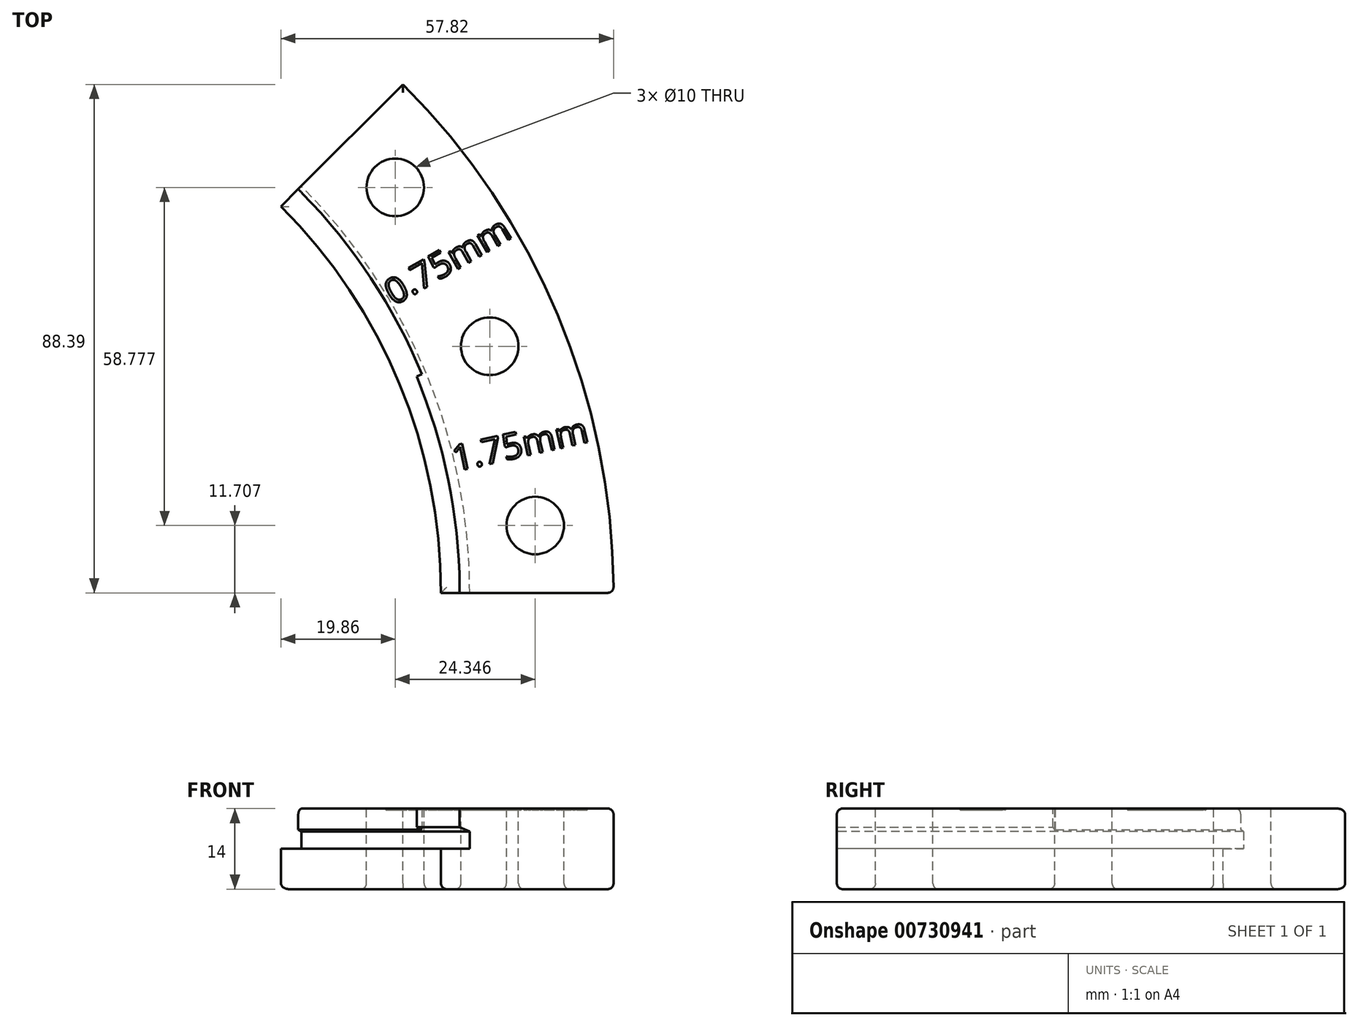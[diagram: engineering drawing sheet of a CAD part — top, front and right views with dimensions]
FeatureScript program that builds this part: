
annotation { "Feature Type Name" : "Feature", "Feature Type Description" : "" }
export const myFeature = defineFeature(function(context is Context, id is Id, definition is map)
    precondition{}
    {
        {
            var Q0;
            Q0=qCreatedBy(makeId("Top.planeOp"),FACE);
            var sketch = newSketch(context, id + "F0", { "sketchPlane" : qUnion([Q0])});
            skCircle(sketch, "E0", {"center": v(0, 0) * mm, "radius": 100 * mm});
            skSolve(sketch);
        }
        {
            var Q0;
            Q0=qCreatedBy(makeId("Front.planeOp"),FACE);
            var sketch = newSketch(context, id + "F1", { "sketchPlane" : qUnion([Q0])});
            skLineSegment(sketch, "E1.0", {"start": v(-100, 0) * mm, "end": v(100, 0) * mm});
            skLineSegment(sketch, "E2", {"start": v(100, 4) * mm, "end": v(97.75, 4) * mm});
            skLineSegment(sketch, "E3", {"start": v(125, 4) * mm, "end": v(100, 4) * mm});
            skLineSegment(sketch, "E4", {"start": v(100, 0) * mm, "end": v(100, -3) * mm});
            skLineSegment(sketch, "E5", {"start": v(100, -10) * mm, "end": v(125, -10) * mm});
            skLineSegment(sketch, "E6", {"start": v(125, -10) * mm, "end": v(125, 4) * mm});
            skLineSegment(sketch, "E7", {"start": v(0, 0) * mm, "end": v(0, 50.74) * mm});
            skLineSegment(sketch, "E8", {"start": v(100, -10) * mm, "end": v(95, -10) * mm});
            skLineSegment(sketch, "E9", {"start": v(95, -10) * mm, "end": v(95, -3) * mm});
            skLineSegment(sketch, "E10", {"start": v(95, -3) * mm, "end": v(100, -3) * mm});
            skLineSegment(sketch, "E11", {"start": v(97.75, 4) * mm, "end": v(97.75, 1) * mm});
            skLineSegment(sketch, "E12", {"start": v(100, 0) * mm, "end": v(97.75, 1) * mm});
            skSolve(sketch);
        }
        {
            var Q0;
            Q0=makeQuery(id+"F1.imprint","IMPRINT",FACE,{"disambiguationData":[TD([[makeQuery(id+"F1.imprint","IMPRINT",EDGE,{"derivedFrom":sQuery(id+"F1.wireOp",EDGE,"E2")}),1.0]])]});
            var Q1;
            Q1=sQuery(id+"F1.wireOp",EDGE,"E7");
            revolve(context, id + "F2", {"entities" : qUnion([Q0]), "axis" : qUnion([Q1]), "revolveType" : RevolveType.ONE_DIRECTION, "angle" : 45 * degree});
        }
        {
            var Q0;
            Q0=makeQuery(id+"F2.opRevolve","CAP_FACE",FACE,{"disambiguationData":[OSD([sQuery(id+"F1.wireOp",EDGE,"E2"),sQuery(id+"F1.wireOp",EDGE,"E3"),sQuery(id+"F1.wireOp",EDGE,"E4"),sQuery(id+"F1.wireOp",EDGE,"E5"),sQuery(id+"F1.wireOp",EDGE,"E6"),sQuery(id+"F1.wireOp",EDGE,"E8"),sQuery(id+"F1.wireOp",EDGE,"E9"),sQuery(id+"F1.wireOp",EDGE,"E10"),sQuery(id+"F1.wireOp",EDGE,"E11"),sQuery(id+"F1.wireOp",EDGE,"E12")])],"isStart":false});
            var sketch = newSketch(context, id + "F3", { "sketchPlane" : qUnion([Q0])});
            skLineSegment(sketch, "E13", {"start": v(0, 0) * mm, "end": v(0, 46.88) * mm});
            skLineSegment(sketch, "E14.0", {"start": v(-99.25, 0.33) * mm, "end": v(-97.75, 1) * mm});
            skLineSegment(sketch, "E15.0", {"start": v(-97.75, 4) * mm, "end": v(-97.75, 1) * mm});
            skLineSegment(sketch, "E16.0", {"start": v(-99.25, 4) * mm, "end": v(-97.75, 4) * mm});
            skLineSegment(sketch, "E17", {"start": v(-99.25, 4) * mm, "end": v(-99.25, 0.33) * mm});
            skLineSegment(sketch, "E18", {"start": v(-97.75, 4) * mm, "end": v(-99.25, 4) * mm});
            skPoint(sketch, "E19.start.orphan", {"position": v(-100, 0) * mm});
            skPoint(sketch, "E20.orphan", {"position": v(-125, 4) * mm});
            skLineSegment(sketch, "E21", {"start": v(-98.25, 4) * mm, "end": v(-98.25, 0.78) * mm});
            skSolve(sketch);
        }
        {
            var Q0;
            Q0=makeQuery(id+"F3.imprint","IMPRINT",FACE,{"disambiguationData":[TD([[makeQuery(id+"F3.imprint","IMPRINT",EDGE,{"derivedFrom":sQuery(id+"F3.wireOp",EDGE,"E15.0")}),-1.0]])]});
            var Q1;
            {var subQ0=sQuery(id+"F3.wireOp",EDGE,"E17");Q1=makeQuery(id+"F3.imprint","IMPRINT",FACE,{"disambiguationData":[TD([[makeQuery(id+"F3.imprint","IMPRINT",EDGE,{"derivedFrom":subQ0}),1.0]])]});}
            var Q2;
            Q2=sQuery(id+"F3.wireOp",EDGE,"E13");
            revolve(context, id + "F4", {"operationType" : NewBodyOperationType.REMOVE, "entities" : qUnion([Q0, Q1]), "axis" : qUnion([Q2]), "revolveType" : RevolveType.ONE_DIRECTION, "oppositeDirection" : true, "angle" : 22.5 * degree, "surfaceOperationType" : NewSurfaceOperationType.NEW});
        }
        {
            var Q0;
            {var subQ0=sQuery(id+"F3.wireOp",EDGE,"E15.0");Q0=makeQuery(id+"F3.imprint","IMPRINT",FACE,{"disambiguationData":[TD([[makeQuery(id+"F3.imprint","IMPRINT",EDGE,{"derivedFrom":subQ0}),-1.0]])]});}
            var Q1;
            Q1=sQuery(id+"F0.wireOp",EDGE,"E0");
            revolve(context, id + "F5", {"operationType" : NewBodyOperationType.REMOVE, "surfaceOperationType" : NewSurfaceOperationType.NEW, "entities" : qUnion([Q0]), "axis" : qUnion([Q1]), "revolveType" : RevolveType.FULL, "oppositeDirection" : true});
        }
        {
            var Q0;
            Q0=makeQuery(id+"F2.opRevolve","SWEPT_FACE",FACE,{"disambiguationData":[OSD([sQuery(id+"F1.wireOp",EDGE,"E2"),sQuery(id+"F1.wireOp",EDGE,"E3")])]});
            var sketch = newSketch(context, id + "F6", { "sketchPlane" : qUnion([Q0])});
            skCircle(sketch, "E22", {"center": v(87.04, 70.48) * mm, "radius": 5 * mm});
            skCircle(sketch, "E23", {"center": v(111.39, 11.7) * mm, "radius": 5 * mm});
            skCircle(sketch, "E24", {"center": v(103.47, 42.86) * mm, "radius": 5 * mm});
            skText(sketch, "E25", { "text": "1.75mm", "fontName": "OpenSans-Regular.ttf"});
            skText(sketch, "E26", { "text": "0.75mm", "fontName": "OpenSans-Regular.ttf"});
            const initialGuessF6  = {"E25": [0.09749, 0.0211, 0.97648, 0.21563, 0.0045], "E26": [0.0868, 0.04986, 0.86603, 0.5, 0.0045]};
            skSetInitialGuess(sketch, initialGuessF6);
            skSolve(sketch);
        }
        {
            var Q0;
            Q0=makeQuery(id+"F6.imprint","IMPRINT",FACE,{"disambiguationData":[TD([[makeQuery(id+"F6.imprint","IMPRINT",EDGE,{"derivedFrom":sQuery(id+"F6.wireOp",EDGE,"E22")}),1.0]])]});
            var Q1;
            Q1=makeQuery(id+"F6.imprint","IMPRINT",FACE,{"disambiguationData":[TD([[makeQuery(id+"F6.imprint","IMPRINT",EDGE,{"derivedFrom":sQuery(id+"F6.wireOp",EDGE,"E24")}),1.0]])]});
            var Q2;
            Q2=makeQuery(id+"F6.imprint","IMPRINT",FACE,{"disambiguationData":[TD([[makeQuery(id+"F6.imprint","IMPRINT",EDGE,{"derivedFrom":sQuery(id+"F6.wireOp",EDGE,"E23")}),1.0]])]});
            extrude(context, id + "F7", {"entities" : qUnion([Q0, Q1, Q2]), "operationType" : NewBodyOperationType.REMOVE, "endBound" : BoundingType.THROUGH_ALL, "oppositeDirection" : true, "depth" : 25 * mm});
        }
        {
            var Q0;
            Q0=qSketchRegion(id+"F6",true);
            extrude(context, id + "F8", {"entities" : qUnion([Q0]), "operationType" : NewBodyOperationType.REMOVE, "oppositeDirection" : true, "depth" : .25 * mm});
        }
        {
            var Q0;
            Q0=makeQuery(id+"F2.opRevolve","CAP_EDGE",EDGE,{"disambiguationData":[OSD([sQuery(id+"F1.wireOp",EDGE,"E2"),sQuery(id+"F1.wireOp",EDGE,"E3")])],"isStart":true});
            var Q1;
            Q1=makeQuery(id+"F2.opRevolve","SWEPT_EDGE",EDGE,{"disambiguationData":[OSD([sQuery(id+"F1.wireOp",EDGE,"E3"),sQuery(id+"F1.wireOp",EDGE,"E6")])]});
            var Q2;
            Q2=makeQuery(id+"F2.opRevolve","CAP_EDGE",EDGE,{"disambiguationData":[OSD([sQuery(id+"F1.wireOp",EDGE,"E2"),sQuery(id+"F1.wireOp",EDGE,"E3")])],"isStart":false});
            var Q3;
            Q3=makeQuery(id+"F2.opRevolve","CAP_EDGE",EDGE,{"disambiguationData":[OSD([sQuery(id+"F1.wireOp",EDGE,"E6")])],"isStart":true});
            var Q4;
            Q4=makeQuery(id+"F2.opRevolve","CAP_EDGE",EDGE,{"disambiguationData":[OSD([sQuery(id+"F1.wireOp",EDGE,"E5"),sQuery(id+"F1.wireOp",EDGE,"E8")])],"isStart":true});
            var Q5;
            Q5=makeQuery(id+"F2.opRevolve","SWEPT_EDGE",EDGE,{"disambiguationData":[OSD([sQuery(id+"F1.wireOp",EDGE,"E5"),sQuery(id+"F1.wireOp",EDGE,"E6")])]});
            var Q6;
            Q6=makeQuery(id+"F2.opRevolve","SWEPT_EDGE",EDGE,{"disambiguationData":[OSD([sQuery(id+"F1.wireOp",EDGE,"E8"),sQuery(id+"F1.wireOp",EDGE,"E9")])]});
            var Q7;
            Q7=makeQuery(id+"F2.opRevolve","CAP_EDGE",EDGE,{"disambiguationData":[OSD([sQuery(id+"F1.wireOp",EDGE,"E5"),sQuery(id+"F1.wireOp",EDGE,"E8")])],"isStart":false});
            var Q8;
            Q8=makeQuery(id+"F7.boolean.opBoolean","COPY",EDGE,{"derivedFrom":makeQuery(id+"F7.opExtrude","CAP_EDGE",EDGE,{"disambiguationData":[OSD([sQuery(id+"F6.wireOp",EDGE,"E22")])],"isStart":true})});
            var Q9;
            Q9=makeQuery(id+"F7.boolean.opBoolean","COPY",EDGE,{"derivedFrom":makeQuery(id+"F7.opExtrude","CAP_EDGE",EDGE,{"disambiguationData":[OSD([sQuery(id+"F6.wireOp",EDGE,"E24")])],"isStart":true})});
            var Q10;
            Q10=makeQuery(id+"F7.boolean.opBoolean","COPY",EDGE,{"derivedFrom":makeQuery(id+"F7.opExtrude","CAP_EDGE",EDGE,{"disambiguationData":[OSD([sQuery(id+"F6.wireOp",EDGE,"E23")])],"isStart":true})});
            var Q11;
            Q11=makeQuery(id+"F7.boolean.opBoolean","INTERSECT",EDGE,{"derivedFrom":[makeQuery(id+"F2.opRevolve","SWEPT_FACE",FACE,{"disambiguationData":[OSD([sQuery(id+"F1.wireOp",EDGE,"E5"),sQuery(id+"F1.wireOp",EDGE,"E8")])]}),makeQuery(id+"F7.opExtrude","SWEPT_FACE",FACE,{"disambiguationData":[OSD([sQuery(id+"F6.wireOp",EDGE,"E23")])]})]});
            var Q12;
            Q12=makeQuery(id+"F7.boolean.opBoolean","INTERSECT",EDGE,{"derivedFrom":[makeQuery(id+"F2.opRevolve","SWEPT_FACE",FACE,{"disambiguationData":[OSD([sQuery(id+"F1.wireOp",EDGE,"E5"),sQuery(id+"F1.wireOp",EDGE,"E8")])]}),makeQuery(id+"F7.opExtrude","SWEPT_FACE",FACE,{"disambiguationData":[OSD([sQuery(id+"F6.wireOp",EDGE,"E24")])]})]});
            var Q13;
            Q13=makeQuery(id+"F7.boolean.opBoolean","INTERSECT",EDGE,{"derivedFrom":[makeQuery(id+"F2.opRevolve","SWEPT_FACE",FACE,{"disambiguationData":[OSD([sQuery(id+"F1.wireOp",EDGE,"E5"),sQuery(id+"F1.wireOp",EDGE,"E8")])]}),makeQuery(id+"F7.opExtrude","SWEPT_FACE",FACE,{"disambiguationData":[OSD([sQuery(id+"F6.wireOp",EDGE,"E22")])]})]});
            fillet(context, id + "F9", {"entities" : qUnion([Q0, Q1, Q2, Q3, Q4, Q5, Q6, Q7, Q8, Q9, Q10, Q11, Q12, Q13]), "radius" : 1 * mm, "tangentPropagation" : true, "allowEdgeOverflow" : false});
        }
    });
